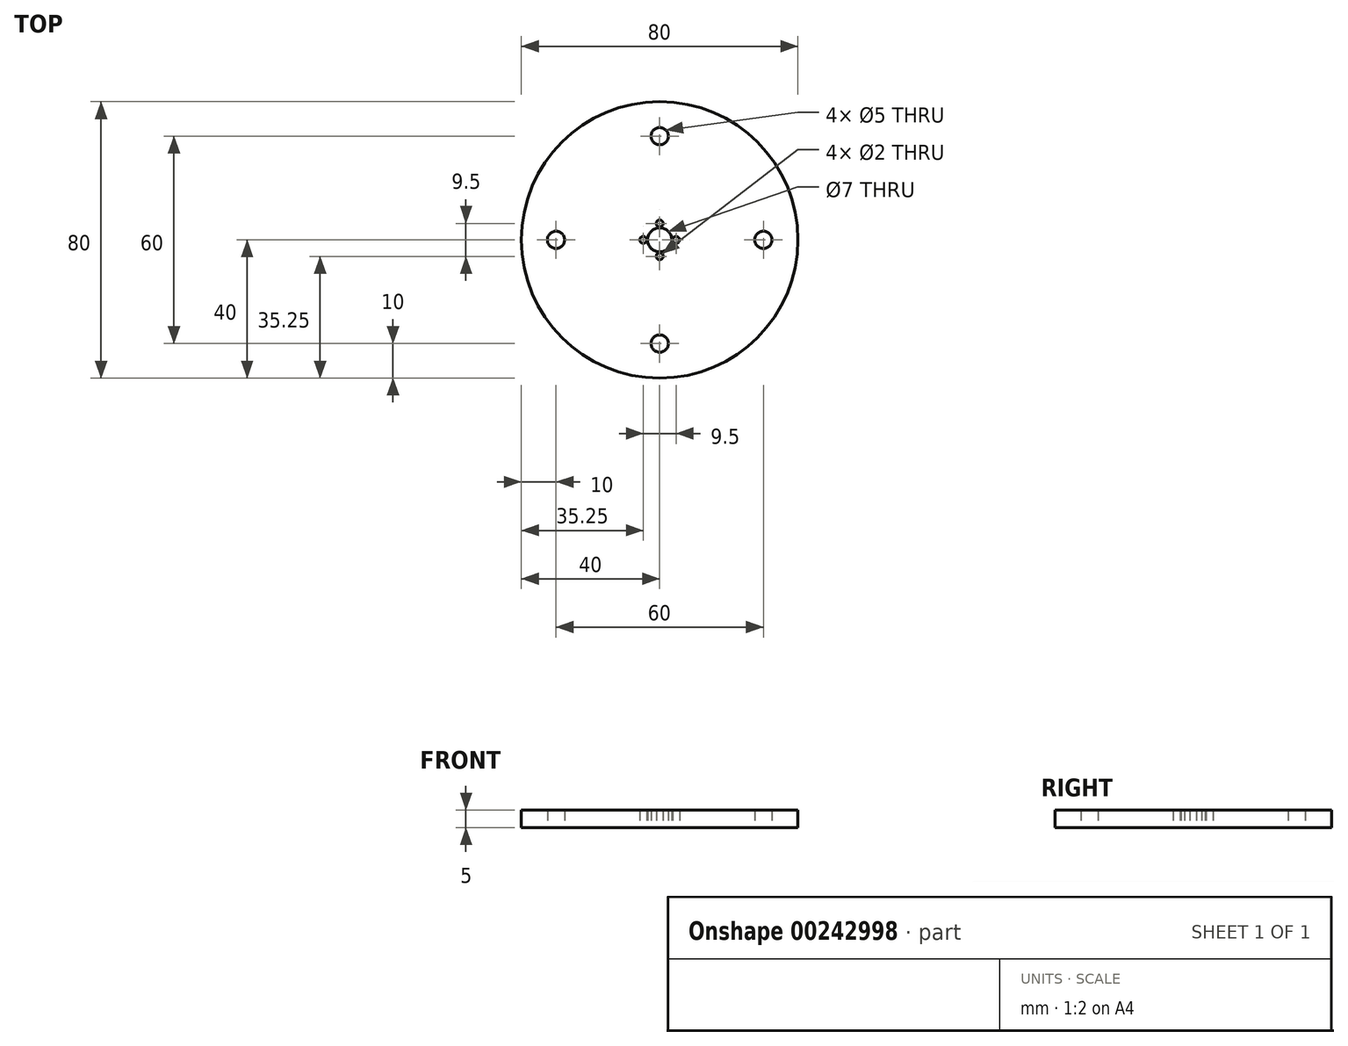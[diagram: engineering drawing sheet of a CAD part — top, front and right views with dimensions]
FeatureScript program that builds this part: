
annotation { "Feature Type Name" : "Feature", "Feature Type Description" : "" }
export const myFeature = defineFeature(function(context is Context, id is Id, definition is map)
    precondition{}
    {
        {
            var Q0;
            Q0=qCreatedBy(makeId("Top.planeOp"),FACE);
            var sketch = newSketch(context, id + "F0", { "sketchPlane" : qUnion([Q0])});
            skCircle(sketch, "E0", {"center": v(0, 0) * mm, "radius": 3.5 * mm});
            skCircle(sketch, "E1", {"center": v(0, 0) * mm, "radius": 4.75 * mm, "construction": true});
            skCircle(sketch, "E2", {"center": v(4.75, 0) * mm, "radius": 1 * mm});
            skCircle(sketch, "E3", {"center": v(0, 4.75) * mm, "radius": 1 * mm});
            skCircle(sketch, "E4", {"center": v(-4.75, 0) * mm, "radius": 1 * mm});
            skCircle(sketch, "E5", {"center": v(0, -4.75) * mm, "radius": 1 * mm});
            skCircle(sketch, "E6", {"center": v(0, 0) * mm, "radius": 30 * mm, "construction": true});
            skCircle(sketch, "E7", {"center": v(0, 0) * mm, "radius": 40 * mm});
            skCircle(sketch, "E8", {"center": v(30, 0) * mm, "radius": 2.5 * mm});
            skCircle(sketch, "E9", {"center": v(0, 30) * mm, "radius": 2.5 * mm});
            skCircle(sketch, "E10", {"center": v(-30, 0) * mm, "radius": 2.5 * mm});
            skCircle(sketch, "E11", {"center": v(0, -30) * mm, "radius": 2.5 * mm});
            skCircle(sketch, "E12", {"center": v(0, 0) * mm, "radius": 15 * mm});
            skSolve(sketch);
        }
        {
            var Q0;
            Q0=makeQuery(id+"F0.imprint","IMPRINT",FACE,{"disambiguationData":[TD([[makeQuery(id+"F0.imprint","IMPRINT",EDGE,{"derivedFrom":sQuery(id+"F0.wireOp",EDGE,"E0")}),-1.0]])]});
            var Q1;
            Q1=makeQuery(id+"F0.imprint","IMPRINT",FACE,{"disambiguationData":[TD([[makeQuery(id+"F0.imprint","IMPRINT",EDGE,{"derivedFrom":sQuery(id+"F0.wireOp",EDGE,"E7")}),1.0]])]});
            extrude(context, id + "F1", {"entities" : qUnion([Q0, Q1]), "depth" : 5 * mm});
        }
    });
